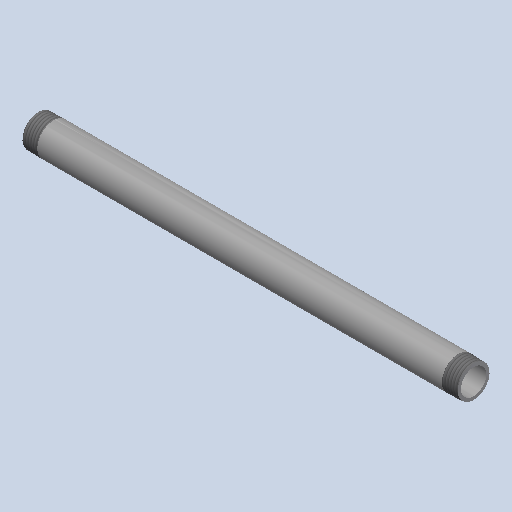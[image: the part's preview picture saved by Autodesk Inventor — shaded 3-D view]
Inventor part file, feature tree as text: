
AUTODESK INVENTOR PART (.ipt)
format: ipt  version: 2025 (Build 290162000, 162)  size: 178,688 bytes
history: native  units: mm (DEFAULTED — no unit token found)
features: other x8, revolve x1
ambient origin geometry x8: Origin, YZ Plane, XZ Plane, XY Plane, X Axis, Y Axis, Z Axis, Center Point
bodies: Solid1 (feature_tree)
feature tree (9):
  revolve  "Revolution1"  [1 undecoded]
  other  "Work Axis1"
  other  "Work Point5"
  other  "Work Axis2"
  other  "Work Point6"
  other  "Work Axis3"
  other  "Work Axis4"
  other  "Work Point7"
  other  "Work Point8"
note: 1 required parameter value undecoded (feature->parameter linkage not recoverable at this tier; creation-order binding heuristic only, values carry confidence <= 0.55)
